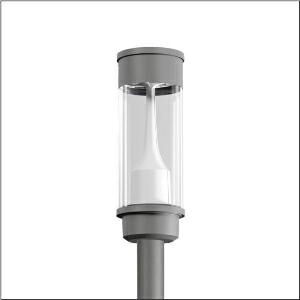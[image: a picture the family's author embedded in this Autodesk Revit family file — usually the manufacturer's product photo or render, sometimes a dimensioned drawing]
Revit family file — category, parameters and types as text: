
# Revit family: litepole_iq___pl1_2s_5xa5415jf14h000022_dba0
name_source: partatom
category: Lighting Fixtures
units: mm (PartAtom-declared; Revit-internal decimal feet)

## family parameters
Cut with Voids When Loaded = No
Host = Face
Light Source = No
Part Type = Normal
Room Calculation Point = No
Round Connector Dimension = Use Diameter
Shared = No

## types (1)
- --- (1 x LED, 2970 lm, 19.3 W, 3000K)
    Apparent Load = 19 VA
    CIE Flux Codes = 23 62 94 96 100
    Color Rendering = 70
    Color Temperature = 3000K
    Default Elevation = 1800 mm
    Description = Litepole iQ, mast luminaire, Module 540 iQ-SR, primary light control with 3 zone facetted reflector, of plastic, silver coated, highly specular, structured, primary optical cover: cover, of PMMA, transparent, light distribution: PL1.2s, light emission: direct distribution, primary light characteristic: symmetric, installation type: post-top, LED, High Power LED, rated luminous flux: 2.970lm, luminous efficacy: 154lm/W, light colour: 730, colour temperature: 3000K, control gear: ECG iQ, control: Street-Remote, Auto-Match, Temp-Guard, Lumen-Switch, Night-Set, Smart-Wire, Light-Fading, Desk-Remote (wireless, voltage-free reading and setting of iQ features in the workshop via application-optimized NFC function/RFID function), optimised constant luminous flux control (CLO 2.0), presetting dimming logarithmic, mains connection: 230..240V, AC, 50/60Hz, connection cable pre-assembled, cable length: 5,5m, wiring characteristics: H07RN-F, start of lifetime: 19W, end of service life: 21W, reduction: 10W, luminaire housing, upper part, of glass-fibre reinforced polyester, coated, Siteco® metallic grey (DB 702S), diameter: 210mm, height: 590mm, spigot size: d x l = 76 x 70mm (post-top) | with reducer (optional accessory) 60 x 70mm, post-top mast mounting element, of diecast aluminium, coated, Siteco® metallic grey (DB 702S), Module 540 iQ-SR, traffic white (RAL 9016), equipment: standard, protection rating (complete): IP65, insulation class (complete): insulation class II (safety insulation), certification: CE, ENEC, VDE, packaging unit: 1 piece

Light Distribution: PL1.2s
    Height = 590 mm
    Lamp = 1 x LED
    Lamp Light Flux = 2970 lm
    Lamp Power = 19.3 W
    Lamp count = 1
    Length = 220 mm
    Luminous efficacy = 154 lm/W
    Manufacturer = Siteco
    ModVariant = No
    Model = 5XA5415JF14H000022
    Number of Poles = 1
    OnlyDefault = Yes
    Power Factor = 1
    Product Name = Litepole iQ | PL1.2s
    Product group = mast luminaire | pylon top
    ProductGroupID = 6100
    Protection Class = Protection class II
    Protection Degree = IP 65
    RLX_Detail_Level = 1
    RLX_Emergency_Light_Flux = 0 lm
    RLX_Emergency_Type = 0
    RLX_Emergency_Type_DB = No
    RlxData = <blob elided: 39889 chars, md5=a83fe0be>
    Socket = socket
    Standby Power = 0 W
    System Light Flux = 2970 lm
    System Power = 19 W
    Type Comments = factory setting: luminous flux: 100 % | dim-lin: 254 | 403 mA
    Type Image = l_1006025.jpg
    URL = http://relux.com
    VarID = @adj_094251
    Voltage = 0 V
    Weight = 0.00 kg
    Width = 0 mm  [stored 0 ft]

note: [stored X ft] marks values corroborated as IEEE doubles in the binary element streams (Revit-internal decimal feet)

## geometry (parser evidence)
native form markers: Blend x4, Sweep x8
no freeform markers — native parametric forms only
